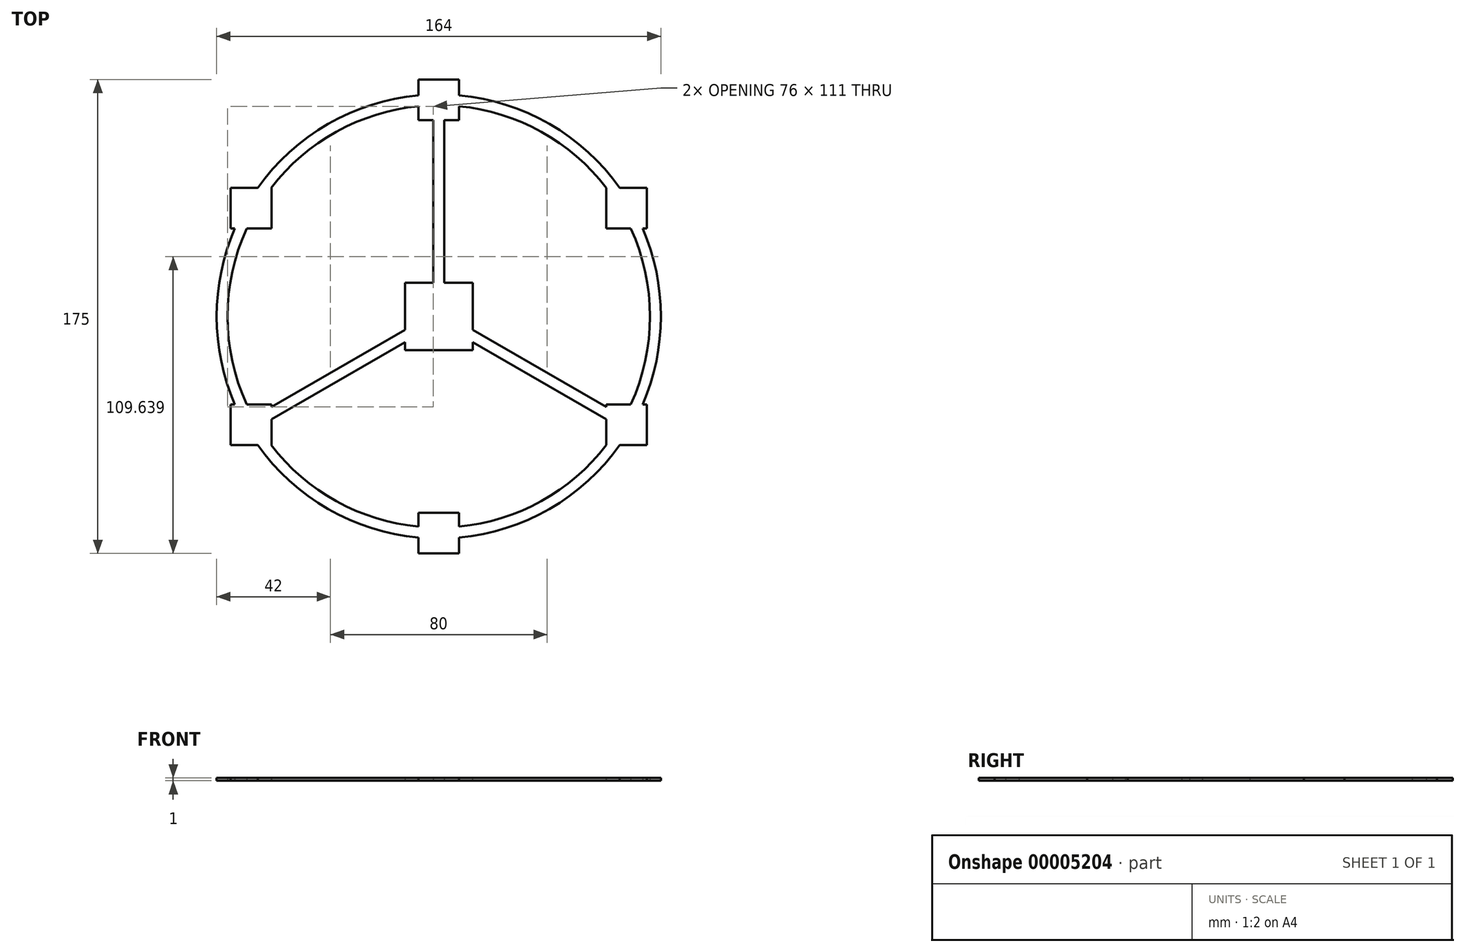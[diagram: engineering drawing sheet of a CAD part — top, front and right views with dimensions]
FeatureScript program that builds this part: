
annotation { "Feature Type Name" : "Feature", "Feature Type Description" : "" }
export const myFeature = defineFeature(function(context is Context, id is Id, definition is map)
    precondition{}
    {
        {
            var Q0;
            Q0=qCreatedBy(makeId("Top.planeOp"),FACE);
            var sketch = newSketch(context, id + "F0", { "sketchPlane" : qUnion([Q0])});
            skCircle(sketch, "E0", {"center": v(0, 0) * mm, "radius": 80 * mm, "construction": true});
            skLineSegment(sketch, "E1", {"start": v(0, 0) * mm, "end": v(0, 80) * mm, "construction": true});
            skCircle(sketch, "E2", {"center": v(0, 0) * mm, "radius": 82 * mm});
            skCircle(sketch, "E3", {"center": v(0, 0) * mm, "radius": 78 * mm});
            skSolve(sketch);
        }
        {
            var Q0;
            Q0 = qSketchRegion(id + "F0", true);
            extrude(context, id + "F1", {"entities" : qUnion([Q0]), "depth" : 1 * mm, "offsetDistance" : 25 * mm});
        }
        {
            var Q0;
            Q0=makeQuery(id+"F1.opExtrude","CAP_FACE",FACE,{"disambiguationData":[OSD([sQuery(id+"F0.wireOp",EDGE,"E2"),sQuery(id+"F0.wireOp",EDGE,"E3")])],"isStart":false});
            var sketch = newSketch(context, id + "F2", { "sketchPlane" : qUnion([Q0])});
            skCircle(sketch, "E4", {"center": v(0, 0) * mm, "radius": 80 * mm, "construction": true});
            skLineSegment(sketch, "E5", {"start": v(0, 0) * mm, "end": v(0, 80) * mm, "construction": true});
            skCircle(sketch, "E6", {"center": v(0, 80) * mm, "radius": 7.5 * mm});
            skCircle(sketch, "E7.1.0", {"center": v(-69.28, 40) * mm, "radius": 7.5 * mm});
            skCircle(sketch, "E7.2.0", {"center": v(-69.28, -40) * mm, "radius": 7.5 * mm});
            skCircle(sketch, "E7.3.0", {"center": v(0, -80) * mm, "radius": 7.5 * mm});
            skCircle(sketch, "E7.4.0", {"center": v(69.28, -40) * mm, "radius": 7.5 * mm});
            skCircle(sketch, "E7.5.0", {"center": v(69.28, 40) * mm, "radius": 7.5 * mm});
            skSolve(sketch);
        }
        {
            var Q0;
            Q0 = qSketchRegion(id + "F2", true);
            var Q1;
            Q1=makeQuery(id+"F1.opExtrude","CAP_FACE",FACE,{"disambiguationData":[OSD([sQuery(id+"F0.wireOp",EDGE,"E2"),sQuery(id+"F0.wireOp",EDGE,"E3")])],"isStart":true});
            extrude(context, id + "F3", {"entities" : qUnion([Q0]), "operationType" : NewBodyOperationType.ADD, "endBound" : BoundingType.UP_TO_SURFACE, "oppositeDirection" : true, "depth" : 25 * mm, "endBoundEntityFace" : qUnion([Q1]), "offsetDistance" : 25 * mm});
        }
        {
            var Q0;
            Q0=makeQuery(id+"F3.boolean.opBoolean","MERGE",FACE,{"derivedFrom":[makeQuery(id+"F1.opExtrude","CAP_FACE",FACE,{"disambiguationData":[OSD([sQuery(id+"F0.wireOp",EDGE,"E2"),sQuery(id+"F0.wireOp",EDGE,"E3")])],"isStart":false}),makeQuery(id+"F3.opExtrude","CAP_FACE",FACE,{"disambiguationData":[OSD([sQuery(id+"F2.wireOp",EDGE,"E6")])],"isStart":true}),makeQuery(id+"F3.opExtrude","CAP_FACE",FACE,{"disambiguationData":[OSD([sQuery(id+"F2.wireOp",EDGE,"E7.1.0")])],"isStart":true}),makeQuery(id+"F3.opExtrude","CAP_FACE",FACE,{"disambiguationData":[OSD([sQuery(id+"F2.wireOp",EDGE,"E7.2.0")])],"isStart":true}),makeQuery(id+"F3.opExtrude","CAP_FACE",FACE,{"disambiguationData":[OSD([sQuery(id+"F2.wireOp",EDGE,"E7.3.0")])],"isStart":true}),makeQuery(id+"F3.opExtrude","CAP_FACE",FACE,{"disambiguationData":[OSD([sQuery(id+"F2.wireOp",EDGE,"E7.4.0")])],"isStart":true}),makeQuery(id+"F3.opExtrude","CAP_FACE",FACE,{"disambiguationData":[OSD([sQuery(id+"F2.wireOp",EDGE,"E7.5.0")])],"isStart":true})]});
            var sketch = newSketch(context, id + "F4", { "sketchPlane" : qUnion([Q0])});
            skCircle(sketch, "E8", {"center": v(0, 0) * mm, "radius": 80 * mm, "construction": true});
            skLineSegment(sketch, "E9", {"start": v(0, 0) * mm, "end": v(0, 80) * mm, "construction": true});
            skLineSegment(sketch, "E10.bottom", {"start": v(2, 72.77) * mm, "end": v(-2, 72.77) * mm});
            skLineSegment(sketch, "E10.top", {"start": v(2, 7.23) * mm, "end": v(-2, 7.23) * mm});
            skLineSegment(sketch, "E10.left", {"start": v(2, 72.77) * mm, "end": v(2, 7.23) * mm});
            skLineSegment(sketch, "E10.right", {"start": v(-2, 72.77) * mm, "end": v(-2, 7.23) * mm});
            skPoint(sketch, "E10.middle", {"position": v(0, 40) * mm});
            skLineSegment(sketch, "E11.1.0", {"start": v(-62.02, -38.12) * mm, "end": v(-5.26, -5.35) * mm});
            skLineSegment(sketch, "E11.1.1", {"start": v(-64.02, -34.65) * mm, "end": v(-62.02, -38.12) * mm});
            skLineSegment(sketch, "E11.1.2", {"start": v(-64.02, -34.65) * mm, "end": v(-7.26, -1.88) * mm});
            skLineSegment(sketch, "E11.1.3", {"start": v(-7.26, -1.88) * mm, "end": v(-5.26, -5.35) * mm});
            skLineSegment(sketch, "E11.2.0", {"start": v(64.02, -34.65) * mm, "end": v(7.26, -1.88) * mm});
            skLineSegment(sketch, "E11.2.1", {"start": v(62.02, -38.12) * mm, "end": v(64.02, -34.65) * mm});
            skLineSegment(sketch, "E11.2.2", {"start": v(62.02, -38.12) * mm, "end": v(5.26, -5.35) * mm});
            skLineSegment(sketch, "E11.2.3", {"start": v(5.26, -5.35) * mm, "end": v(7.26, -1.88) * mm});
            skSolve(sketch);
        }
        {
            var Q0;
            Q0 = qSketchRegion(id + "F4", true);
            var Q1;
            Q1=makeQuery(id+"F3.boolean.opBoolean","MERGE",FACE,{"derivedFrom":[makeQuery(id+"F1.opExtrude","CAP_FACE",FACE,{"disambiguationData":[OSD([sQuery(id+"F0.wireOp",EDGE,"E2"),sQuery(id+"F0.wireOp",EDGE,"E3")])],"isStart":true}),makeQuery(id+"F3.opExtrude","CAP_FACE",FACE,{"disambiguationData":[OSD([sQuery(id+"F2.wireOp",EDGE,"E6")])],"isStart":false}),makeQuery(id+"F3.opExtrude","CAP_FACE",FACE,{"disambiguationData":[OSD([sQuery(id+"F2.wireOp",EDGE,"E7.1.0")])],"isStart":false}),makeQuery(id+"F3.opExtrude","CAP_FACE",FACE,{"disambiguationData":[OSD([sQuery(id+"F2.wireOp",EDGE,"E7.2.0")])],"isStart":false}),makeQuery(id+"F3.opExtrude","CAP_FACE",FACE,{"disambiguationData":[OSD([sQuery(id+"F2.wireOp",EDGE,"E7.3.0")])],"isStart":false}),makeQuery(id+"F3.opExtrude","CAP_FACE",FACE,{"disambiguationData":[OSD([sQuery(id+"F2.wireOp",EDGE,"E7.4.0")])],"isStart":false}),makeQuery(id+"F3.opExtrude","CAP_FACE",FACE,{"disambiguationData":[OSD([sQuery(id+"F2.wireOp",EDGE,"E7.5.0")])],"isStart":false})]});
            extrude(context, id + "F5", {"entities" : qUnion([Q0]), "operationType" : NewBodyOperationType.ADD, "endBound" : BoundingType.UP_TO_SURFACE, "oppositeDirection" : true, "depth" : 25 * mm, "endBoundEntityFace" : qUnion([Q1]), "offsetDistance" : 25 * mm});
        }
        {
            var Q0;
            Q0=makeQuery(id+"F5.boolean.opBoolean","MERGE",FACE,{"derivedFrom":[makeQuery(id+"F3.boolean.opBoolean","MERGE",FACE,{"derivedFrom":[makeQuery(id+"F1.opExtrude","CAP_FACE",FACE,{"disambiguationData":[OSD([sQuery(id+"F0.wireOp",EDGE,"E2"),sQuery(id+"F0.wireOp",EDGE,"E3")])],"isStart":false}),makeQuery(id+"F3.opExtrude","CAP_FACE",FACE,{"disambiguationData":[OSD([sQuery(id+"F2.wireOp",EDGE,"E6")])],"isStart":true}),makeQuery(id+"F3.opExtrude","CAP_FACE",FACE,{"disambiguationData":[OSD([sQuery(id+"F2.wireOp",EDGE,"E7.1.0")])],"isStart":true}),makeQuery(id+"F3.opExtrude","CAP_FACE",FACE,{"disambiguationData":[OSD([sQuery(id+"F2.wireOp",EDGE,"E7.2.0")])],"isStart":true}),makeQuery(id+"F3.opExtrude","CAP_FACE",FACE,{"disambiguationData":[OSD([sQuery(id+"F2.wireOp",EDGE,"E7.3.0")])],"isStart":true}),makeQuery(id+"F3.opExtrude","CAP_FACE",FACE,{"disambiguationData":[OSD([sQuery(id+"F2.wireOp",EDGE,"E7.4.0")])],"isStart":true}),makeQuery(id+"F3.opExtrude","CAP_FACE",FACE,{"disambiguationData":[OSD([sQuery(id+"F2.wireOp",EDGE,"E7.5.0")])],"isStart":true})]}),makeQuery(id+"F5.opExtrude","CAP_FACE",FACE,{"disambiguationData":[OSD([sQuery(id+"F4.wireOp",EDGE,"E10.bottom"),sQuery(id+"F4.wireOp",EDGE,"E10.top"),sQuery(id+"F4.wireOp",EDGE,"E10.left"),sQuery(id+"F4.wireOp",EDGE,"E10.right")])],"isStart":true}),makeQuery(id+"F5.opExtrude","CAP_FACE",FACE,{"disambiguationData":[OSD([sQuery(id+"F4.wireOp",EDGE,"E11.1.0"),sQuery(id+"F4.wireOp",EDGE,"E11.1.1"),sQuery(id+"F4.wireOp",EDGE,"E11.1.2"),sQuery(id+"F4.wireOp",EDGE,"E11.1.3")])],"isStart":true}),makeQuery(id+"F5.opExtrude","CAP_FACE",FACE,{"disambiguationData":[OSD([sQuery(id+"F4.wireOp",EDGE,"E11.2.0"),sQuery(id+"F4.wireOp",EDGE,"E11.2.1"),sQuery(id+"F4.wireOp",EDGE,"E11.2.2"),sQuery(id+"F4.wireOp",EDGE,"E11.2.3")])],"isStart":true})]});
            var sketch = newSketch(context, id + "F6", { "sketchPlane" : qUnion([Q0])});
            skCircle(sketch, "E12", {"center": v(0, 0) * mm, "radius": 12.5 * mm});
            skSolve(sketch);
        }
        {
            var Q0;
            Q0 = qSketchRegion(id + "F6", true);
            var Q1;
            Q1=makeQuery(id+"F5.boolean.opBoolean","MERGE",FACE,{"derivedFrom":[makeQuery(id+"F3.boolean.opBoolean","MERGE",FACE,{"derivedFrom":[makeQuery(id+"F1.opExtrude","CAP_FACE",FACE,{"disambiguationData":[OSD([sQuery(id+"F0.wireOp",EDGE,"E2"),sQuery(id+"F0.wireOp",EDGE,"E3")])],"isStart":true}),makeQuery(id+"F3.opExtrude","CAP_FACE",FACE,{"disambiguationData":[OSD([sQuery(id+"F2.wireOp",EDGE,"E6")])],"isStart":false}),makeQuery(id+"F3.opExtrude","CAP_FACE",FACE,{"disambiguationData":[OSD([sQuery(id+"F2.wireOp",EDGE,"E7.1.0")])],"isStart":false}),makeQuery(id+"F3.opExtrude","CAP_FACE",FACE,{"disambiguationData":[OSD([sQuery(id+"F2.wireOp",EDGE,"E7.2.0")])],"isStart":false}),makeQuery(id+"F3.opExtrude","CAP_FACE",FACE,{"disambiguationData":[OSD([sQuery(id+"F2.wireOp",EDGE,"E7.3.0")])],"isStart":false}),makeQuery(id+"F3.opExtrude","CAP_FACE",FACE,{"disambiguationData":[OSD([sQuery(id+"F2.wireOp",EDGE,"E7.4.0")])],"isStart":false}),makeQuery(id+"F3.opExtrude","CAP_FACE",FACE,{"disambiguationData":[OSD([sQuery(id+"F2.wireOp",EDGE,"E7.5.0")])],"isStart":false})]}),makeQuery(id+"F5.opExtrude","CAP_FACE",FACE,{"disambiguationData":[OSD([sQuery(id+"F4.wireOp",EDGE,"E10.bottom"),sQuery(id+"F4.wireOp",EDGE,"E10.top"),sQuery(id+"F4.wireOp",EDGE,"E10.left"),sQuery(id+"F4.wireOp",EDGE,"E10.right")])],"isStart":false}),makeQuery(id+"F5.opExtrude","CAP_FACE",FACE,{"disambiguationData":[OSD([sQuery(id+"F4.wireOp",EDGE,"E11.1.0"),sQuery(id+"F4.wireOp",EDGE,"E11.1.1"),sQuery(id+"F4.wireOp",EDGE,"E11.1.2"),sQuery(id+"F4.wireOp",EDGE,"E11.1.3")])],"isStart":false}),makeQuery(id+"F5.opExtrude","CAP_FACE",FACE,{"disambiguationData":[OSD([sQuery(id+"F4.wireOp",EDGE,"E11.2.0"),sQuery(id+"F4.wireOp",EDGE,"E11.2.1"),sQuery(id+"F4.wireOp",EDGE,"E11.2.2"),sQuery(id+"F4.wireOp",EDGE,"E11.2.3")])],"isStart":false})]});
            extrude(context, id + "F7", {"entities" : qUnion([Q0]), "operationType" : NewBodyOperationType.ADD, "endBound" : BoundingType.UP_TO_SURFACE, "oppositeDirection" : true, "depth" : 25 * mm, "endBoundEntityFace" : qUnion([Q1]), "offsetDistance" : 25 * mm});
        }
        {
            var Q0;
            Q0=makeQuery(id+"F7.boolean.opBoolean","MERGE",FACE,{"derivedFrom":[makeQuery(id+"F5.boolean.opBoolean","MERGE",FACE,{"derivedFrom":[makeQuery(id+"F3.boolean.opBoolean","MERGE",FACE,{"derivedFrom":[makeQuery(id+"F1.opExtrude","CAP_FACE",FACE,{"disambiguationData":[OSD([sQuery(id+"F0.wireOp",EDGE,"E2"),sQuery(id+"F0.wireOp",EDGE,"E3")])],"isStart":false}),makeQuery(id+"F3.opExtrude","CAP_FACE",FACE,{"disambiguationData":[OSD([sQuery(id+"F2.wireOp",EDGE,"E6")])],"isStart":true}),makeQuery(id+"F3.opExtrude","CAP_FACE",FACE,{"disambiguationData":[OSD([sQuery(id+"F2.wireOp",EDGE,"E7.1.0")])],"isStart":true}),makeQuery(id+"F3.opExtrude","CAP_FACE",FACE,{"disambiguationData":[OSD([sQuery(id+"F2.wireOp",EDGE,"E7.2.0")])],"isStart":true}),makeQuery(id+"F3.opExtrude","CAP_FACE",FACE,{"disambiguationData":[OSD([sQuery(id+"F2.wireOp",EDGE,"E7.3.0")])],"isStart":true}),makeQuery(id+"F3.opExtrude","CAP_FACE",FACE,{"disambiguationData":[OSD([sQuery(id+"F2.wireOp",EDGE,"E7.4.0")])],"isStart":true}),makeQuery(id+"F3.opExtrude","CAP_FACE",FACE,{"disambiguationData":[OSD([sQuery(id+"F2.wireOp",EDGE,"E7.5.0")])],"isStart":true})]}),makeQuery(id+"F5.opExtrude","CAP_FACE",FACE,{"disambiguationData":[OSD([sQuery(id+"F4.wireOp",EDGE,"E10.bottom"),sQuery(id+"F4.wireOp",EDGE,"E10.top"),sQuery(id+"F4.wireOp",EDGE,"E10.left"),sQuery(id+"F4.wireOp",EDGE,"E10.right")])],"isStart":true}),makeQuery(id+"F5.opExtrude","CAP_FACE",FACE,{"disambiguationData":[OSD([sQuery(id+"F4.wireOp",EDGE,"E11.1.0"),sQuery(id+"F4.wireOp",EDGE,"E11.1.1"),sQuery(id+"F4.wireOp",EDGE,"E11.1.2"),sQuery(id+"F4.wireOp",EDGE,"E11.1.3")])],"isStart":true}),makeQuery(id+"F5.opExtrude","CAP_FACE",FACE,{"disambiguationData":[OSD([sQuery(id+"F4.wireOp",EDGE,"E11.2.0"),sQuery(id+"F4.wireOp",EDGE,"E11.2.1"),sQuery(id+"F4.wireOp",EDGE,"E11.2.2"),sQuery(id+"F4.wireOp",EDGE,"E11.2.3")])],"isStart":true})]}),makeQuery(id+"F7.opExtrude","CAP_FACE",FACE,{"disambiguationData":[OSD([sQuery(id+"F6.wireOp",EDGE,"E12")])],"isStart":true})]});
            var sketch = newSketch(context, id + "F8", { "sketchPlane" : qUnion([Q0])});
            skLineSegment(sketch, "E13.bottom", {"start": v(12.5, 12.5) * mm, "end": v(-12.5, 12.5) * mm});
            skLineSegment(sketch, "E13.top", {"start": v(12.5, -12.5) * mm, "end": v(-12.5, -12.5) * mm});
            skLineSegment(sketch, "E13.left", {"start": v(12.5, 12.5) * mm, "end": v(12.5, -12.5) * mm});
            skLineSegment(sketch, "E13.right", {"start": v(-12.5, 12.5) * mm, "end": v(-12.5, -12.5) * mm});
            skPoint(sketch, "E13.middle", {"position": v(0, 0) * mm});
            skLineSegment(sketch, "E14.bottom", {"start": v(76.78, 47.5) * mm, "end": v(61.78, 47.5) * mm});
            skLineSegment(sketch, "E14.top", {"start": v(76.78, 32.5) * mm, "end": v(61.78, 32.5) * mm});
            skLineSegment(sketch, "E14.left", {"start": v(76.78, 47.5) * mm, "end": v(76.78, 32.5) * mm});
            skLineSegment(sketch, "E14.right", {"start": v(61.78, 47.5) * mm, "end": v(61.78, 32.5) * mm});
            skPoint(sketch, "E14.middle", {"position": v(69.28, 40) * mm});
            skLineSegment(sketch, "E15.bottom", {"start": v(7.5, 87.5) * mm, "end": v(-7.5, 87.5) * mm});
            skLineSegment(sketch, "E15.top", {"start": v(7.5, 72.5) * mm, "end": v(-7.5, 72.5) * mm});
            skLineSegment(sketch, "E15.left", {"start": v(7.5, 87.5) * mm, "end": v(7.5, 72.5) * mm});
            skLineSegment(sketch, "E15.right", {"start": v(-7.5, 87.5) * mm, "end": v(-7.5, 72.5) * mm});
            skPoint(sketch, "E15.middle", {"position": v(0, 80) * mm});
            skLineSegment(sketch, "E16.bottom", {"start": v(-61.78, 47.5) * mm, "end": v(-76.78, 47.5) * mm});
            skLineSegment(sketch, "E16.top", {"start": v(-61.78, 32.5) * mm, "end": v(-76.78, 32.5) * mm});
            skLineSegment(sketch, "E16.left", {"start": v(-61.78, 47.5) * mm, "end": v(-61.78, 32.5) * mm});
            skLineSegment(sketch, "E16.right", {"start": v(-76.78, 47.5) * mm, "end": v(-76.78, 32.5) * mm});
            skPoint(sketch, "E16.middle", {"position": v(-69.28, 40) * mm});
            skLineSegment(sketch, "E17.bottom", {"start": v(-61.78, -32.5) * mm, "end": v(-76.78, -32.5) * mm});
            skLineSegment(sketch, "E17.top", {"start": v(-61.78, -47.5) * mm, "end": v(-76.78, -47.5) * mm});
            skLineSegment(sketch, "E17.left", {"start": v(-61.78, -32.5) * mm, "end": v(-61.78, -47.5) * mm});
            skLineSegment(sketch, "E17.right", {"start": v(-76.78, -32.5) * mm, "end": v(-76.78, -47.5) * mm});
            skPoint(sketch, "E17.middle", {"position": v(-69.28, -40) * mm});
            skLineSegment(sketch, "E18.bottom", {"start": v(7.5, -72.5) * mm, "end": v(-7.5, -72.5) * mm});
            skLineSegment(sketch, "E18.top", {"start": v(7.5, -87.5) * mm, "end": v(-7.5, -87.5) * mm});
            skLineSegment(sketch, "E18.left", {"start": v(7.5, -72.5) * mm, "end": v(7.5, -87.5) * mm});
            skLineSegment(sketch, "E18.right", {"start": v(-7.5, -72.5) * mm, "end": v(-7.5, -87.5) * mm});
            skPoint(sketch, "E18.middle", {"position": v(0, -80) * mm});
            skLineSegment(sketch, "E19.bottom", {"start": v(76.78, -32.5) * mm, "end": v(61.78, -32.5) * mm});
            skLineSegment(sketch, "E19.top", {"start": v(76.78, -47.5) * mm, "end": v(61.78, -47.5) * mm});
            skLineSegment(sketch, "E19.left", {"start": v(76.78, -32.5) * mm, "end": v(76.78, -47.5) * mm});
            skLineSegment(sketch, "E19.right", {"start": v(61.78, -32.5) * mm, "end": v(61.78, -47.5) * mm});
            skPoint(sketch, "E19.middle", {"position": v(69.28, -40) * mm});
            skSolve(sketch);
        }
        {
            var Q0;
            Q0 = qSketchRegion(id + "F8", true);
            var Q1;
            Q1=makeQuery(id+"F7.boolean.opBoolean","MERGE",FACE,{"derivedFrom":[makeQuery(id+"F5.boolean.opBoolean","MERGE",FACE,{"derivedFrom":[makeQuery(id+"F3.boolean.opBoolean","MERGE",FACE,{"derivedFrom":[makeQuery(id+"F1.opExtrude","CAP_FACE",FACE,{"disambiguationData":[OSD([sQuery(id+"F0.wireOp",EDGE,"E2"),sQuery(id+"F0.wireOp",EDGE,"E3")])],"isStart":true}),makeQuery(id+"F3.opExtrude","CAP_FACE",FACE,{"disambiguationData":[OSD([sQuery(id+"F2.wireOp",EDGE,"E6")])],"isStart":false}),makeQuery(id+"F3.opExtrude","CAP_FACE",FACE,{"disambiguationData":[OSD([sQuery(id+"F2.wireOp",EDGE,"E7.1.0")])],"isStart":false}),makeQuery(id+"F3.opExtrude","CAP_FACE",FACE,{"disambiguationData":[OSD([sQuery(id+"F2.wireOp",EDGE,"E7.2.0")])],"isStart":false}),makeQuery(id+"F3.opExtrude","CAP_FACE",FACE,{"disambiguationData":[OSD([sQuery(id+"F2.wireOp",EDGE,"E7.3.0")])],"isStart":false}),makeQuery(id+"F3.opExtrude","CAP_FACE",FACE,{"disambiguationData":[OSD([sQuery(id+"F2.wireOp",EDGE,"E7.4.0")])],"isStart":false}),makeQuery(id+"F3.opExtrude","CAP_FACE",FACE,{"disambiguationData":[OSD([sQuery(id+"F2.wireOp",EDGE,"E7.5.0")])],"isStart":false})]}),makeQuery(id+"F5.opExtrude","CAP_FACE",FACE,{"disambiguationData":[OSD([sQuery(id+"F4.wireOp",EDGE,"E10.bottom"),sQuery(id+"F4.wireOp",EDGE,"E10.top"),sQuery(id+"F4.wireOp",EDGE,"E10.left"),sQuery(id+"F4.wireOp",EDGE,"E10.right")])],"isStart":false}),makeQuery(id+"F5.opExtrude","CAP_FACE",FACE,{"disambiguationData":[OSD([sQuery(id+"F4.wireOp",EDGE,"E11.1.0"),sQuery(id+"F4.wireOp",EDGE,"E11.1.1"),sQuery(id+"F4.wireOp",EDGE,"E11.1.2"),sQuery(id+"F4.wireOp",EDGE,"E11.1.3")])],"isStart":false}),makeQuery(id+"F5.opExtrude","CAP_FACE",FACE,{"disambiguationData":[OSD([sQuery(id+"F4.wireOp",EDGE,"E11.2.0"),sQuery(id+"F4.wireOp",EDGE,"E11.2.1"),sQuery(id+"F4.wireOp",EDGE,"E11.2.2"),sQuery(id+"F4.wireOp",EDGE,"E11.2.3")])],"isStart":false})]}),makeQuery(id+"F7.opExtrude","CAP_FACE",FACE,{"disambiguationData":[OSD([sQuery(id+"F6.wireOp",EDGE,"E12")])],"isStart":false})]});
            extrude(context, id + "F9", {"entities" : qUnion([Q0]), "operationType" : NewBodyOperationType.ADD, "endBound" : BoundingType.UP_TO_SURFACE, "oppositeDirection" : true, "depth" : 1.5 * mm, "endBoundEntityFace" : qUnion([Q1]), "offsetDistance" : 25 * mm});
        }
    });
